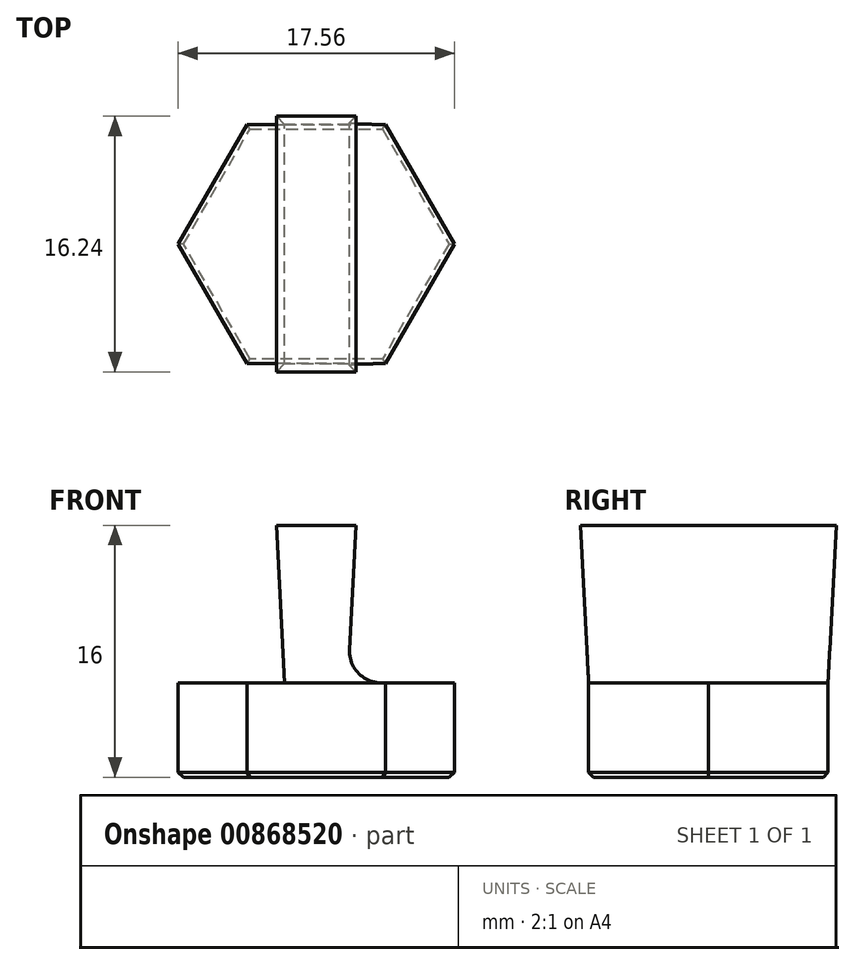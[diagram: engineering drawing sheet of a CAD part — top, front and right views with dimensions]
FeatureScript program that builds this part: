
annotation { "Feature Type Name" : "Feature", "Feature Type Description" : "" }
export const myFeature = defineFeature(function(context is Context, id is Id, definition is map)
    precondition{}
    {
        {
            var Q0;
            Q0=qCreatedBy(makeId("Top.planeOp"),FACE);
            var sketch = newSketch(context, id + "F0", { "sketchPlane" : qUnion([Q0])});
            skCircle(sketch, "E0.cCircle", {"center": v(0, 0) * mm, "radius": 7.6 * mm, "construction": true});
            skLineSegment(sketch, "E0.0", {"start": v(8.78, 0) * mm, "end": v(4.39, -7.6) * mm});
            skLineSegment(sketch, "E0.1", {"start": v(4.39, -7.6) * mm, "end": v(-4.39, -7.6) * mm});
            skLineSegment(sketch, "E0.2", {"start": v(-4.39, -7.6) * mm, "end": v(-8.78, 0) * mm});
            skLineSegment(sketch, "E0.3", {"start": v(-8.78, 0) * mm, "end": v(-4.39, 7.6) * mm});
            skLineSegment(sketch, "E0.4", {"start": v(-4.39, 7.6) * mm, "end": v(4.39, 7.6) * mm});
            skLineSegment(sketch, "E0.5", {"start": v(4.39, 7.6) * mm, "end": v(8.78, 0) * mm});
            skPoint(sketch, "E0.0.midPoint", {"position": v(6.58, -3.8) * mm});
            skSolve(sketch);
        }
        {
            var Q0;
            Q0=makeQuery(id+"F0.imprint","IMPRINT",FACE,{"disambiguationData":[TD([[makeQuery(id+"F0.imprint","IMPRINT",EDGE,{"derivedFrom":sQuery(id+"F0.wireOp",EDGE,"E0.0")}),-1.0]])]});
            extrude(context, id + "F1", {"entities" : qUnion([Q0]), "depth" : 6 * mm, "offsetDistance" : 25 * mm});
        }
        {
            var Q0;
            Q0=makeQuery(id+"F1.opExtrude","CAP_FACE",FACE,{"disambiguationData":[OSD([sQuery(id+"F0.wireOp",EDGE,"E0.0"),sQuery(id+"F0.wireOp",EDGE,"E0.1"),sQuery(id+"F0.wireOp",EDGE,"E0.2"),sQuery(id+"F0.wireOp",EDGE,"E0.3"),sQuery(id+"F0.wireOp",EDGE,"E0.4"),sQuery(id+"F0.wireOp",EDGE,"E0.5")])],"isStart":false});
            var sketch = newSketch(context, id + "F2", { "sketchPlane" : qUnion([Q0])});
            skLineSegment(sketch, "E1.bottom", {"start": v(-2, 7.6) * mm, "end": v(2, 7.6) * mm});
            skLineSegment(sketch, "E1.top", {"start": v(-2, -7.6) * mm, "end": v(2, -7.6) * mm});
            skLineSegment(sketch, "E1.left", {"start": v(-2, 7.6) * mm, "end": v(-2, -7.6) * mm});
            skLineSegment(sketch, "E1.right", {"start": v(2, 7.6) * mm, "end": v(2, -7.6) * mm});
            skLineSegment(sketch, "E2", {"start": v(-10.81, 0) * mm, "end": v(10.19, 0) * mm, "construction": true});
            skLineSegment(sketch, "E3", {"start": v(0, 10.8) * mm, "end": v(0, -10.84) * mm, "construction": true});
            skPoint(sketch, "E3.endSnap0", {"position": v(0, -7.6) * mm});
            skSolve(sketch);
        }
        {
            var Q0;
            Q0=makeQuery(id+"F2.imprint","IMPRINT",FACE,{"disambiguationData":[TD([[makeQuery(id+"F2.imprint","IMPRINT",EDGE,{"derivedFrom":sQuery(id+"F2.wireOp",EDGE,"E1.bottom")}),-1.0]])]});
            extrude(context, id + "F3", {"entities" : qUnion([Q0]), "operationType" : NewBodyOperationType.ADD, "depth" : 10 * mm, "offsetDistance" : 25 * mm, "hasDraft" : true, "draftAngle" : 3 * degree});
        }
        {
            var Q0;
            Q0=makeQuery(id+"F3.opExtrude","CAP_EDGE",EDGE,{"disambiguationData":[OSD([sQuery(id+"F2.wireOp",EDGE,"E1.right")])],"isStart":true});
            var Q1;
            Q1=makeQuery(id+"F3.opExtrude","CAP_EDGE",EDGE,{"disambiguationData":[OSD([sQuery(id+"F2.wireOp",EDGE,"E1.left")])],"isStart":true});
            fillet(context, id + "F4", {"entities" : qUnion([Q0, Q1]), "radius" : 2 * mm, "tangentPropagation" : true, "allowEdgeOverflow" : false});
        }
        {
            var Q0;
            Q0=makeQuery(id+"F1.opExtrude","CAP_FACE",FACE,{"disambiguationData":[OSD([sQuery(id+"F0.wireOp",EDGE,"E0.0"),sQuery(id+"F0.wireOp",EDGE,"E0.1"),sQuery(id+"F0.wireOp",EDGE,"E0.2"),sQuery(id+"F0.wireOp",EDGE,"E0.3"),sQuery(id+"F0.wireOp",EDGE,"E0.4"),sQuery(id+"F0.wireOp",EDGE,"E0.5")])],"isStart":true});
            chamfer(context, id + "F5", {"entities" : qUnion([Q0]), "width" : 0.3 * mm, "tangentPropagation" : true});
        }
    });
